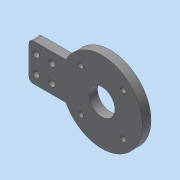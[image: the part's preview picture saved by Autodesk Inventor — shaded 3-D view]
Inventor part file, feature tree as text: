
AUTODESK INVENTOR PART (.ipt)
format: ipt  version: 2017 (Build 210142000, 142)  size: 134,656 bytes
history: native  units: in
note: dims shown in document units (in); Inventor stores cm internally (conversion verified against a paired STEP export)
features: other x8, extrude x2, sketch x1
ambient origin geometry x8: Origin, YZ Plane, XZ Plane, XY Plane, X Axis, Y Axis, Z Axis, Center Point
bodies: Solid1 (feature_tree)
feature tree (11):
  sketch  "Sketch1"  dims[d0=2.3228in d2=0.125in d9=0.816in d10=0.19in d13=0.7874in d15=0.45in d16=0.7874in d18=0.5in d21=0.1575in d23=0.1575in d24=0.1575in d25=0.1575in d26=45.0deg d27=0.25in d28=0.0in d29=1.0in d30=0.0in d31=1.0in d32=0.0in d33=1.0in d34=0.0in d35=1.0in d36=0.0in d37=1.0in d38=0.0in d39=1.0in d40=0.0in d41=1.0in d42=0.0in d43=1.0in d44=0.0in d45=0.75in d46=1.0in d47=0.0in d48=1.2205in d49=1.2205in d50=1.2205in d51=0.2in d52=1.06in d53=0.6102in]
  extrude  "plate"  Depth=0.125in
  extrude  "motor hole"  Depth=0.25in
  other  "platethread1"
  other  "platethread2"
  other  "platethread3"
  other  "platethread4"
  other  "motorthread1"
  other  "motorthread2"
  other  "motorthread3"
  other  "motorthread4"
